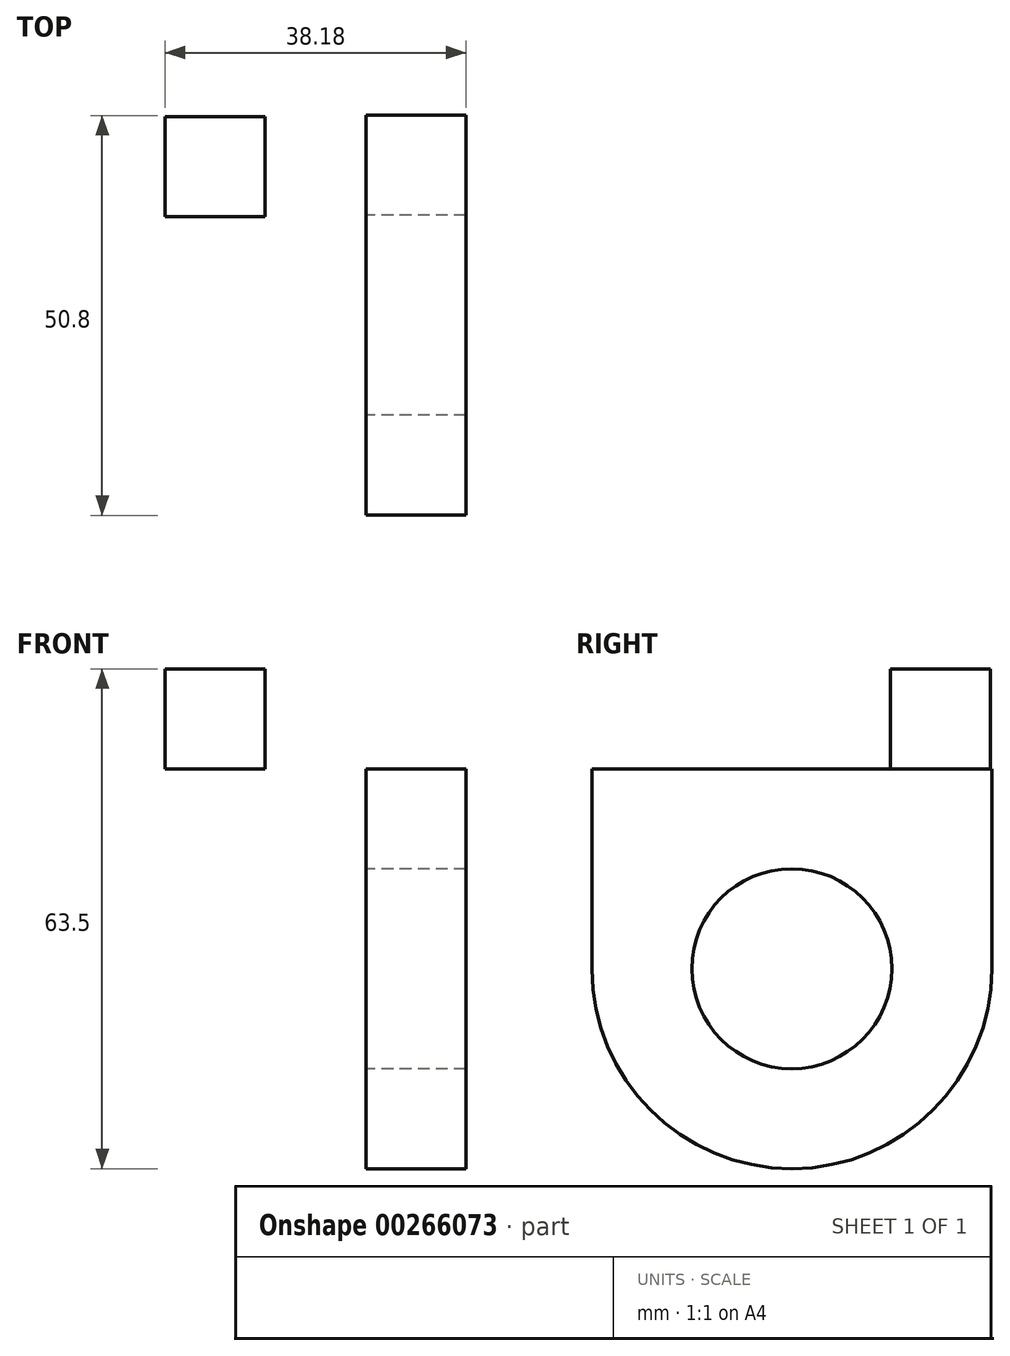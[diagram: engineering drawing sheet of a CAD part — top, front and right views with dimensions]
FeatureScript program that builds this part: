
annotation { "Feature Type Name" : "Feature", "Feature Type Description" : "" }
export const myFeature = defineFeature(function(context is Context, id is Id, definition is map)
    precondition{}
    {
        {
            var Q0;
            Q0=qCreatedBy(makeId("Top.planeOp"),FACE);
            var sketch = newSketch(context, id + "F0", { "sketchPlane" : qUnion([Q0])});
            skLineSegment(sketch, "E0.bottom", {"start": v(19.05, 25.4) * mm, "end": v(-19.05, 25.4) * mm});
            skLineSegment(sketch, "E0.top", {"start": v(19.05, -25.4) * mm, "end": v(-19.05, -25.4) * mm});
            skLineSegment(sketch, "E0.left", {"start": v(19.05, 25.4) * mm, "end": v(19.05, -25.4) * mm});
            skLineSegment(sketch, "E0.right", {"start": v(-19.05, 25.4) * mm, "end": v(-19.05, -25.4) * mm});
            skPoint(sketch, "E0.middle", {"position": v(0, 0) * mm});
            skLineSegment(sketch, "E1.bottom", {"start": v(-19.05, 25.4) * mm, "end": v(-6.35, 25.4) * mm});
            skLineSegment(sketch, "E1.top", {"start": v(-19.05, 12.7) * mm, "end": v(-6.35, 12.7) * mm});
            skLineSegment(sketch, "E1.left", {"start": v(-19.05, 25.4) * mm, "end": v(-19.05, 12.7) * mm});
            skLineSegment(sketch, "E1.right", {"start": v(-6.35, 25.4) * mm, "end": v(-6.35, 12.7) * mm});
            skSolve(sketch);
        }
        {
            var Q0;
            Q0=makeQuery(id+"F0.imprint","IMPRINT",FACE,{"disambiguationData":[TD([[makeQuery(id+"F0.imprint","IMPRINT",EDGE,{"derivedFrom":sQuery(id+"F0.wireOp",EDGE,"E0.bottom")}),1.0]])]});
            extrude(context, id + "F1", {"entities" : qUnion([Q0]), "depth" : 12.7 * mm});
        }
        {
            var Q0;
            Q0=qCreatedBy(makeId("Top.planeOp"),FACE);
            var sketch = newSketch(context, id + "F2", { "sketchPlane" : qUnion([Q0])});
            skLineSegment(sketch, "E2.bottom", {"start": v(19.13, -25.22) * mm, "end": v(6.43, -25.22) * mm});
            skLineSegment(sketch, "E2.top", {"start": v(19.13, 25.58) * mm, "end": v(6.43, 25.58) * mm});
            skLineSegment(sketch, "E2.left", {"start": v(19.13, -25.22) * mm, "end": v(19.13, 25.58) * mm});
            skLineSegment(sketch, "E2.right", {"start": v(6.43, -25.22) * mm, "end": v(6.43, 25.58) * mm});
            skSolve(sketch);
        }
        {
            var Q0;
            Q0=makeQuery(id+"F2.imprint","IMPRINT",FACE,{"disambiguationData":[TD([[makeQuery(id+"F2.imprint","IMPRINT",EDGE,{"derivedFrom":sQuery(id+"F2.wireOp",EDGE,"E2.bottom")}),-1.0]])]});
            extrude(context, id + "F3", {"entities" : qUnion([Q0]), "operationType" : NewBodyOperationType.ADD, "oppositeDirection" : true, "depth" : 50.8 * mm});
        }
        {
            var Q0;
            Q0=qCreatedBy(makeId("Right.planeOp"),FACE);
            var sketch = newSketch(context, id + "F4", { "sketchPlane" : qUnion([Q0])});
            skCircle(sketch, "E3", {"center": v(0.18, -25.4) * mm, "radius": 12.7 * mm});
            skArc(sketch, "E4", {"start": v(25.74, -25.36) * mm, "mid": v(-17.8, -7.88) * mm, "end": v(0, -51.29) * mm});
            skSolve(sketch);
        }
        {
            var Q0;
            Q0=makeQuery(id+"F4.imprint","IMPRINT",FACE,{"disambiguationData":[TD([[makeQuery(id+"F4.imprint","IMPRINT",EDGE,{"derivedFrom":sQuery(id+"F4.wireOp",EDGE,"E3")}),1.0]])]});
            extrude(context, id + "F5", {"entities" : qUnion([Q0]), "operationType" : NewBodyOperationType.REMOVE, "depth" : 21.59 * mm});
        }
        {
            var Q0;
            Q0=makeQuery(id+"F3.opExtrude","SWEPT_FACE",FACE,{"disambiguationData":[OSD([sQuery(id+"F2.wireOp",EDGE,"E2.right")])]});
            var sketch = newSketch(context, id + "F6", { "sketchPlane" : qUnion([Q0])});
            skArc(sketch, "E5", {"start": v(-25.58, -25.4) * mm, "mid": v(-0.18, -50.8) * mm, "end": v(25.22, -25.4) * mm});
            skLineSegment(sketch, "E6", {"start": v(-25.58, -25.4) * mm, "end": v(-25.58, -50.8) * mm});
            skLineSegment(sketch, "E7", {"start": v(-25.58, -50.8) * mm, "end": v(25.22, -50.8) * mm});
            skLineSegment(sketch, "E8", {"start": v(25.22, -50.8) * mm, "end": v(25.22, -25.4) * mm});
            skSolve(sketch);
        }
        {
            var Q0;
            Q0 = qSketchRegion(id + "F6", true);
            extrude(context, id + "F7", {"entities" : qUnion([Q0]), "operationType" : NewBodyOperationType.REMOVE, "oppositeDirection" : true, "depth" : 25.4 * mm});
        }
    });
